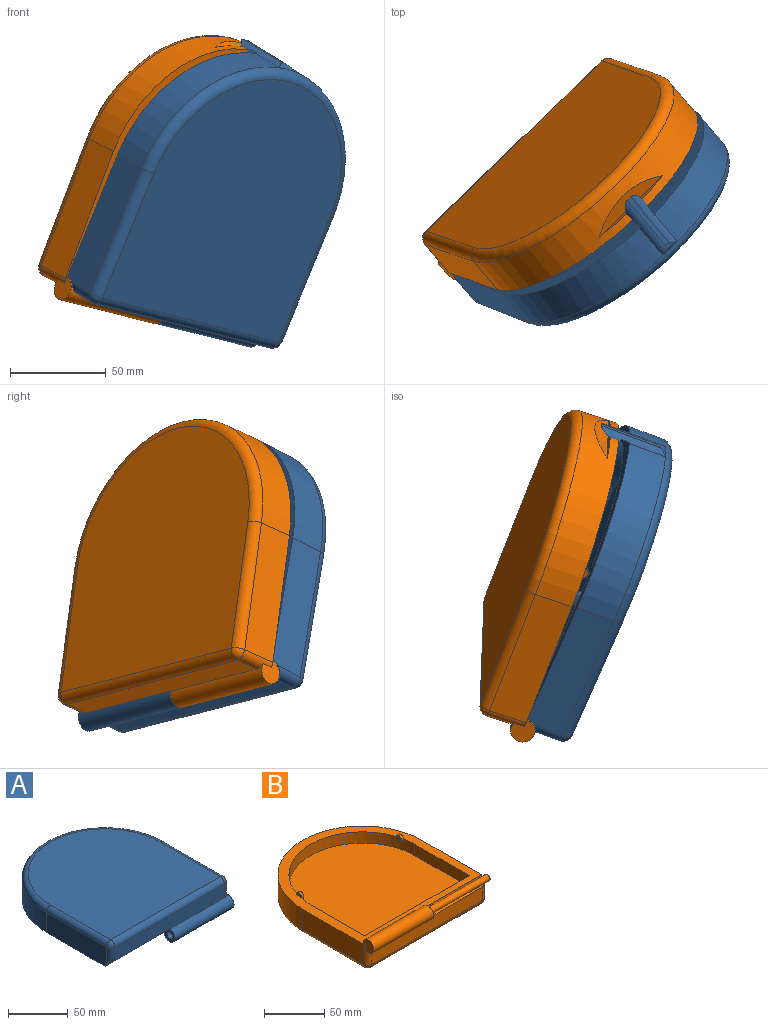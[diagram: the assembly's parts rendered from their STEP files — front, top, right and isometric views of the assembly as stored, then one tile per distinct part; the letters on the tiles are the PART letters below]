
ASSEMBLY  parts=2 mates=1
PART A: 38 faces, bbox 151.2x158.2x42.2 mm
  f0: cylinder r=3.17mm len=6.35mm, axis (-1,0,0), area 105.3mm2, adj f1,f2,f8,f34,f37
  f1: plane 139.94x139.7mm, normal (0,0,-1), area 3771.8mm2, adj f0,f2,f4,f5,f6,f8,f9,f10
  f2: cylinder r=61.12mm len=122.24mm, axis (0,0,-1), area 2428.4mm2, adj f0,f1,f8,f10,f11,f35
  f3: plane 129.54x13.97mm, normal (0,-1,0), area 1789.1mm2, adj f12,f13,f14,f18,f20,f22
  f4: plane 71.12x20.32mm, normal (-1,0,0), area 1440.5mm2, adj f1,f6,f12,f15,f22
  f5: plane 82.55x26.67mm, normal (1,0,0), area 1536.9mm2, adj f1,f6,f14,f17,f18,f23
  f6: cylinder r=69.85mm len=139.7mm, axis (0,0,-1), area 4241.4mm2, adj f1,f4,f5,f16,f30,f31,f32
  f7: plane 135.89x129.54mm, normal (0,0,1), area 15802.6mm2, adj f15,f16,f17,f20
  f8: plane 63.5x12.7mm, normal (1,0,0), area 798.5mm2, adj f0,f1,f2,f9,f11
  f9: plane 122.24x12.7mm, normal (0,1,0), area 1552.4mm2, adj f1,f8,f10,f11
  f10: plane 63.5x12.7mm, normal (-1,0,0), area 798.5mm2, adj f1,f2,f9,f11,f35
  f11: plane 124.62x122.24mm, normal (0,0,-1), area 13629.8mm2, adj f2,f8,f9,f10
  f12: cylinder r=6.67mm len=69.85mm, axis (1,0,0), area 716.9mm2, adj f1,f3,f4,f13,f22
  f13: plane 13.02x13.02mm, normal (-1,0,0), area 98.3mm2, adj f1,f3,f12,f14,f23
  f14: cylinder r=6.35mm len=69.85mm, axis (-1,0,0), area 2105.1mm2, adj f1,f3,f5,f13,f18
  f15: cylinder r=5.08mm len=71.12mm, axis (0,1,0), area 567.5mm2, adj f4,f7,f16,f21
  f16: torus R=64.77mm, axis (0,0,1), area 1704.8mm2, adj f6,f7,f15,f17
  f17: cylinder r=5.08mm len=71.12mm, axis (0,-1,0), area 567.5mm2, adj f5,f7,f16,f19
  f18: cylinder r=5.08mm len=16.51mm, axis (0,0,1), area 121.6mm2, adj f3,f5,f14,f19
  f19: sphere r=5.08mm, area 25.8mm2, adj f17,f18,f20
  f20: cylinder r=5.08mm len=129.54mm, axis (-1,0,0), area 1033.7mm2, adj f3,f7,f19,f21
  f21: sphere r=5.08mm, area 40.5mm2, adj f15,f20,f22
  f22: cylinder r=5.08mm len=16mm, axis (0,0,-1), area 118.3mm2, adj f3,f4,f12,f21
  f23: cylinder r=3.17mm len=69.85mm, axis (-1,0,0), area 1393.4mm2, adj f5,f13
  f24: plane 1.03x0.48mm, normal (1,0,0), area 0.2mm2, adj f27,f28,f30
  f25: plane 1.03x0.48mm, normal (-1,0,0), area 0.2mm2, adj f27,f28,f31
  f26: plane 10.04x4.86mm, normal (0,-1,0), area 48.7mm2, adj f1,f27,f30,f31
  f27: plane 12.7x3.91mm, normal (0,0,1), area 46.8mm2, adj f24,f25,f26,f28,f30,f31
  f28: plane 12.7x11.93mm, normal (0,-0.91,-0.42), area 140.9mm2, adj f24,f25,f27,f29,f30,f31
  f29: plane 33.02x2.54mm, normal (0,1,0), area 83.9mm2, adj f28,f30,f31,f32
  f30: cylinder r=5.08mm len=36.97mm, axis (0,0,-1), area 171.4mm2, adj f1,f6,f24,f26,f27,f28,f29,f32
  f31: cylinder r=5.08mm len=36.97mm, axis (0,0,1), area 171.4mm2, adj f1,f6,f25,f26,f27,f28,f29,f32
  f32: bspline ~21.05x4.47mm, area 30.3mm2, adj f6,f29,f30,f31
  f33: plane 6.35x3.18mm, normal (1,0,0), area 15.8mm2, adj f1,f35
  f34: plane 6.35x3.18mm, normal (-1,0,0), area 15.8mm2, adj f0,f1
  f35: cylinder r=3.17mm len=6.35mm, axis (-1,0,0), area 105.3mm2, adj f1,f2,f10,f33,f36
  f36: plane 6.35x6.35mm, normal (-1,0,0), area 31.7mm2, adj f35
  f37: plane 6.35x6.35mm, normal (1,0,0), area 31.7mm2, adj f0
PART B: 33 faces, bbox 151.2x158.4x31.8 mm
  f0: cylinder r=3.17mm len=6.35mm, axis (-1,0,0), area 45.6mm2, adj f1,f2,f30,f32
  f1: plane 143.54x139.7mm, normal (0,0,1), area 3797.1mm2, adj f0,f2,f4,f5,f6,f8,f9,f10
  f2: cylinder r=61.11mm len=122.22mm, axis (0,0,1), area 2165.4mm2, adj f0,f1,f22,f24,f25,f28,f29,f30
  f3: plane 129.54x13.97mm, normal (0,-1,0), area 1793.7mm2, adj f8,f10,f11,f12,f14,f15
  f4: plane 71.12x20.32mm, normal (1,0,0), area 1441.4mm2, adj f1,f5,f11,f15,f19
  f5: cylinder r=69.85mm len=139.7mm, axis (0,0,1), area 4182.3mm2, adj f1,f4,f6,f18,f26,f27
  f6: plane 71.12x20.32mm, normal (-1,0,0), area 1445.2mm2, adj f1,f5,f12,f16
  f7: plane 135.89x129.54mm, normal (0,0,-1), area 15802.6mm2, adj f14,f16,f18,f19
  f8: cylinder r=6.35mm len=69.85mm, axis (1,0,0), area 2107.4mm2, adj f1,f3,f9,f10,f12
  f9: plane 12.7x12.7mm, normal (-1,0,0), area 111.7mm2, adj f1,f8,f12
  f10: plane 12.99x12.95mm, normal (1,0,0), area 101.5mm2, adj f1,f3,f8,f11,f20
  f11: cylinder r=6.6mm len=69.16mm, axis (-1,0,0), area 700.2mm2, adj f1,f3,f4,f10,f15
  f12: cylinder r=5.08mm len=20.32mm, axis (0,0,1), area 129.3mm2, adj f1,f3,f6,f8,f9,f13
  f13: sphere r=5.08mm, area 40.5mm2, adj f12,f14,f16
  f14: cylinder r=5.08mm len=129.54mm, axis (-1,0,0), area 1033.7mm2, adj f3,f7,f13,f17
  f15: cylinder r=5.08mm len=16.31mm, axis (0,0,1), area 113.8mm2, adj f3,f4,f11,f17
  f16: cylinder r=5.08mm len=71.12mm, axis (0,1,0), area 567.5mm2, adj f6,f7,f13,f18
  f17: sphere r=5.08mm, area 40.5mm2, adj f14,f15,f19
  f18: torus R=64.77mm, axis (0,0,1), area 1704.8mm2, adj f5,f7,f16,f19
  f19: cylinder r=5.08mm len=71.12mm, axis (0,-1,0), area 567.5mm2, adj f4,f7,f17,f18
  f20: cylinder r=2.98mm len=69.85mm, axis (-1,0,0), area 1309.8mm2, adj f10,f21
  f21: plane 5.97x5.97mm, normal (1,0,0), area 28mm2, adj f20
  f22: plane 63.5x11.43mm, normal (1,0,0), area 725.8mm2, adj f1,f2,f23,f25
  f23: plane 122.22x11.43mm, normal (0,1,0), area 1397mm2, adj f1,f22,f24,f25
  f24: plane 63.5x11.43mm, normal (-1,0,0), area 725.8mm2, adj f1,f2,f23,f25
  f25: plane 124.61x122.23mm, normal (0,0,1), area 13627.8mm2, adj f2,f22,f23,f24
  f26: plane 46.9x8.7mm, normal (0,0.91,0.42), area 301.8mm2, adj f5,f27
  f27: plane 46.9x4.05mm, normal (0,0,-1), area 127.5mm2, adj f5,f26
  f28: cylinder r=3.17mm len=6.35mm, axis (-1,0,0), area 43.8mm2, adj f1,f2,f29,f31
  f29: plane 6.35x4.88mm, normal (1,0,0), area 16.4mm2, adj f1,f2,f28
  f30: plane 6.35x5.91mm, normal (-1,0,0), area 18.9mm2, adj f0,f1,f2
  f31: plane 6.35x6.35mm, normal (-1,0,0), area 31.7mm2, adj f28
  f32: plane 6.35x6.35mm, normal (1,0,0), area 31.7mm2, adj f0
PLACE A rot(axis=(0.89,0.42,0.17),113.8deg) t=(-34.13,-190.85,0.51)mm
PLACE B rot(axis=(0.89,0.43,0.18),111.8deg) t=(-36.03,-188.64,1.48)mm fixed
MATE revolute B.f20 <-> A.f12  axis (0.71,0.68,-0.18) through (-13.38,-131.53,-81.56)mm
